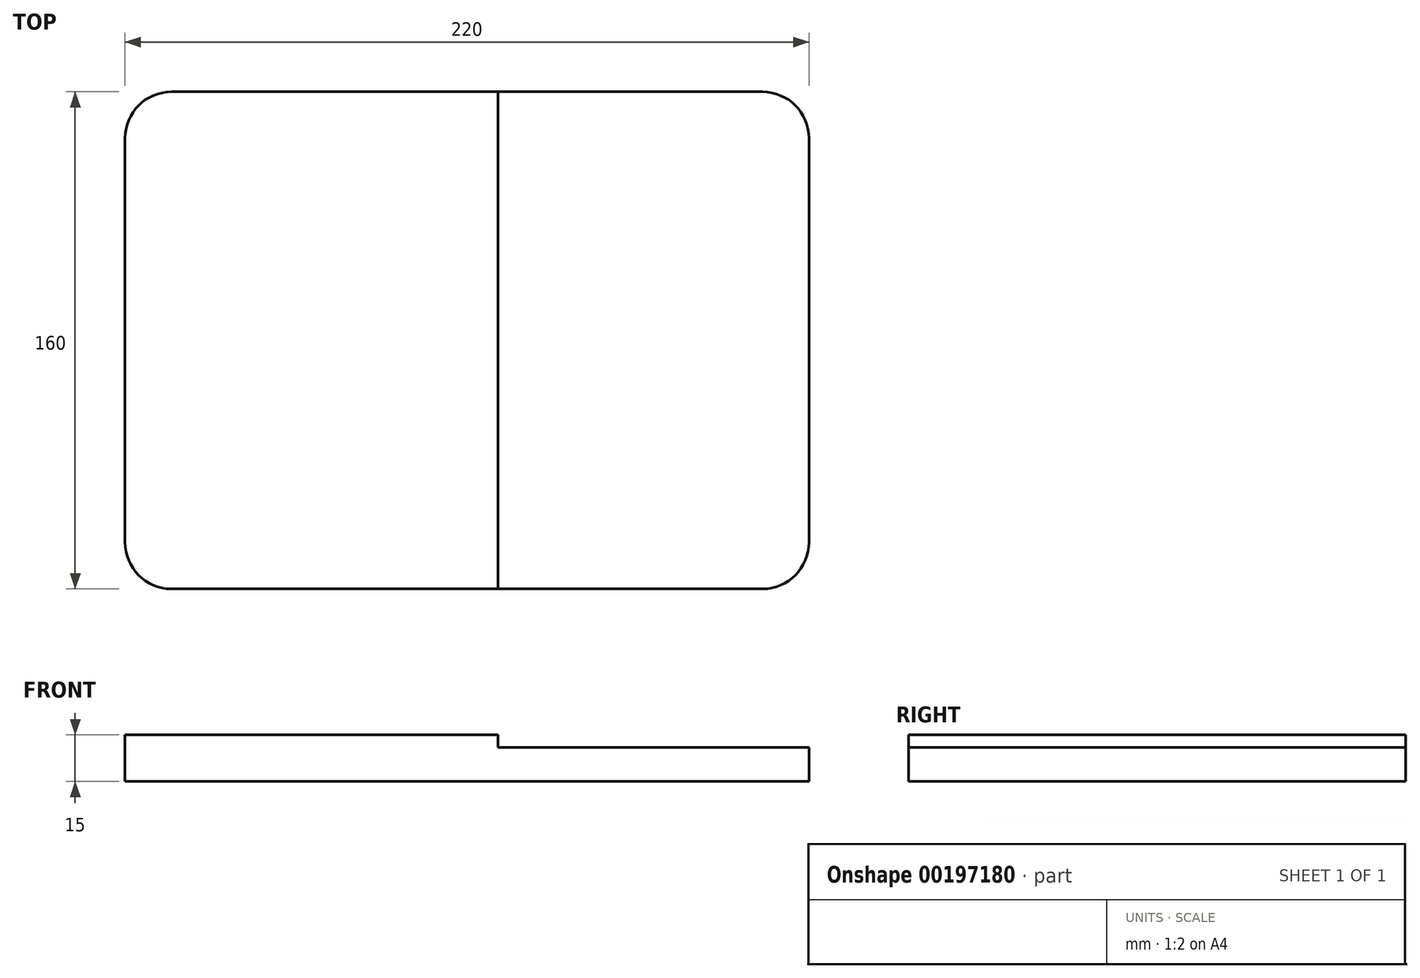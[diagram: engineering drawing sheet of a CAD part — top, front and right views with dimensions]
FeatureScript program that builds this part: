
annotation { "Feature Type Name" : "Feature", "Feature Type Description" : "" }
export const myFeature = defineFeature(function(context is Context, id is Id, definition is map)
    precondition{}
    {
        {
            var Q0;
            Q0=qCreatedBy(makeId("Front.planeOp"),FACE);
            var sketch = newSketch(context, id + "F0", { "sketchPlane" : qUnion([Q0])});
            skLineSegment(sketch, "E0.bottom", {"start": v(110, -7.5) * mm, "end": v(-110, -7.5) * mm});
            skLineSegment(sketch, "E0.top", {"start": v(110, 7.5) * mm, "end": v(-110, 7.5) * mm, "construction": true});
            skLineSegment(sketch, "E0.left", {"start": v(110, -7.5) * mm, "end": v(110, 7.5) * mm});
            skLineSegment(sketch, "E0.right", {"start": v(-110, -7.5) * mm, "end": v(-110, 7.5) * mm});
            skPoint(sketch, "E0.middle", {"position": v(0, 0) * mm});
            skLineSegment(sketch, "E1", {"start": v(10, 7.5) * mm, "end": v(10, 3.5) * mm});
            skLineSegment(sketch, "E2", {"start": v(10, 3.5) * mm, "end": v(110, 3.5) * mm});
            skLineSegment(sketch, "E3", {"start": v(10, 7.5) * mm, "end": v(-110, 7.5) * mm});
            skSolve(sketch);
        }
        {
            var Q0;
            Q0 = qSketchRegion(id + "F0", true);
            extrude(context, id + "F1", {"entities" : qUnion([Q0]), "endBound" : BoundingType.SYMMETRIC, "depth" : 160 * mm});
        }
        {
            var Q0;
            Q0=makeQuery(id+"F1.opExtrude","CAP_EDGE",EDGE,{"disambiguationData":[OSD([sQuery(id+"F0.wireOp",EDGE,"E0.right")])],"isStart":false});
            var Q1;
            Q1=makeQuery(id+"F1.opExtrude","CAP_EDGE",EDGE,{"disambiguationData":[OSD([sQuery(id+"F0.wireOp",EDGE,"E0.left")])],"isStart":false});
            var Q2;
            Q2=makeQuery(id+"F1.opExtrude","CAP_EDGE",EDGE,{"disambiguationData":[OSD([sQuery(id+"F0.wireOp",EDGE,"E0.left")])],"isStart":true});
            var Q3;
            Q3=makeQuery(id+"F1.opExtrude","CAP_EDGE",EDGE,{"disambiguationData":[OSD([sQuery(id+"F0.wireOp",EDGE,"E0.right")])],"isStart":true});
            fillet(context, id + "F2", {"entities" : qUnion([Q0, Q1, Q2, Q3]), "radius" : 15 * mm, "tangentPropagation" : true, "allowEdgeOverflow" : false});
        }
    });
